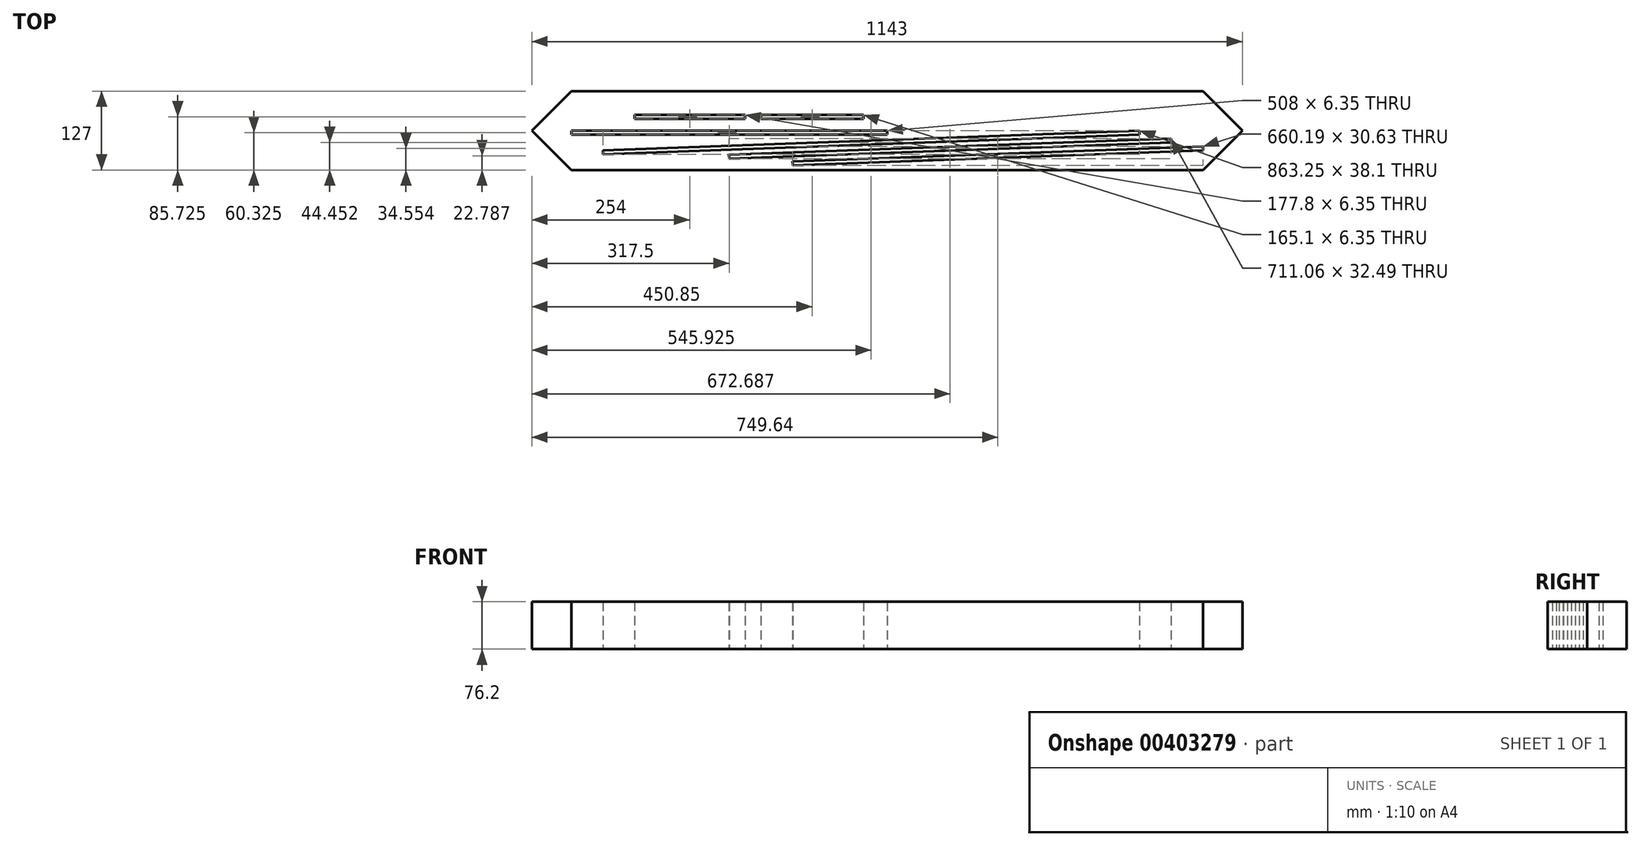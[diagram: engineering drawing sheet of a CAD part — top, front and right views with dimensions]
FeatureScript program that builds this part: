
annotation { "Feature Type Name" : "Feature", "Feature Type Description" : "" }
export const myFeature = defineFeature(function(context is Context, id is Id, definition is map)
    precondition{}
    {
        {
            var Q0;
            Q0=qCreatedBy(makeId("Top.planeOp"),FACE);
            var sketch = newSketch(context, id + "F0", { "sketchPlane" : qUnion([Q0])});
            skLineSegment(sketch, "E0.bottom", {"start": v(-508, 0) * mm, "end": v(508, 0) * mm});
            skLineSegment(sketch, "E0.top", {"start": v(-508, -127) * mm, "end": v(508, -127) * mm});
            skLineSegment(sketch, "E0.left", {"start": v(-508, 0) * mm, "end": v(-508, -127) * mm});
            skLineSegment(sketch, "E0.right", {"start": v(508, 0) * mm, "end": v(508, -127) * mm});
            skPoint(sketch, "E1", {"position": v(-508, -63.5) * mm});
            skPoint(sketch, "E2", {"position": v(508, -63.5) * mm});
            skLineSegment(sketch, "E3", {"start": v(-508, -63.5) * mm, "end": v(508, -63.5) * mm});
            skLineSegment(sketch, "E4", {"start": v(-508, -63.5) * mm, "end": v(-571.5, -63.5) * mm});
            skLineSegment(sketch, "E5", {"start": v(508, -63.5) * mm, "end": v(571.5, -63.5) * mm});
            skLineSegment(sketch, "E6", {"start": v(-571.5, -63.5) * mm, "end": v(-508, 0) * mm});
            skLineSegment(sketch, "E7", {"start": v(-571.5, -63.5) * mm, "end": v(-508, -127) * mm});
            skLineSegment(sketch, "E8", {"start": v(508, -127) * mm, "end": v(571.5, -63.5) * mm});
            skLineSegment(sketch, "E9", {"start": v(571.5, -63.5) * mm, "end": v(508, 0) * mm});
            skLineSegment(sketch, "E10.bottom", {"start": v(-406.4, -38.1) * mm, "end": v(-228.6, -38.1) * mm});
            skLineSegment(sketch, "E10.top", {"start": v(-406.4, -44.45) * mm, "end": v(-228.6, -44.45) * mm});
            skLineSegment(sketch, "E10.left", {"start": v(-406.4, -38.1) * mm, "end": v(-406.4, -44.45) * mm});
            skLineSegment(sketch, "E10.right", {"start": v(-228.6, -38.1) * mm, "end": v(-228.6, -44.45) * mm});
            skLineSegment(sketch, "E11.bottom", {"start": v(-203.2, -38.1) * mm, "end": v(-38.1, -38.1) * mm});
            skLineSegment(sketch, "E11.top", {"start": v(-203.2, -44.45) * mm, "end": v(-38.1, -44.45) * mm});
            skLineSegment(sketch, "E11.left", {"start": v(-203.2, -38.1) * mm, "end": v(-203.2, -44.45) * mm});
            skLineSegment(sketch, "E11.right", {"start": v(-38.1, -38.1) * mm, "end": v(-38.1, -44.45) * mm});
            skLineSegment(sketch, "E12.bottom", {"start": v(-508, -63.5) * mm, "end": v(0, -63.5) * mm});
            skLineSegment(sketch, "E12.top", {"start": v(-508, -69.85) * mm, "end": v(0, -69.85) * mm});
            skLineSegment(sketch, "E12.left", {"start": v(-508, -63.5) * mm, "end": v(-508, -69.85) * mm});
            skLineSegment(sketch, "E12.right", {"start": v(0, -63.5) * mm, "end": v(0, -69.85) * mm});
            skLineSegment(sketch, "E13", {"start": v(-457.2, -95.25) * mm, "end": v(405.82, -63.5) * mm});
            skLineSegment(sketch, "E14", {"start": v(-456.97, -101.6) * mm, "end": v(406.05, -69.85) * mm});
            skLineSegment(sketch, "E15", {"start": v(406.05, -69.85) * mm, "end": v(405.82, -63.5) * mm});
            skLineSegment(sketch, "E16", {"start": v(-457.2, -95.25) * mm, "end": v(-456.97, -101.6) * mm});
            skLineSegment(sketch, "E17", {"start": v(-254, -108.7) * mm, "end": v(456.72, -82.54) * mm});
            skLineSegment(sketch, "E18", {"start": v(456.72, -82.54) * mm, "end": v(456.49, -76.2) * mm});
            skLineSegment(sketch, "E19", {"start": v(456.49, -76.2) * mm, "end": v(-254.34, -102.35) * mm});
            skLineSegment(sketch, "E20", {"start": v(-254, -108.7) * mm, "end": v(-254.34, -102.35) * mm});
            skLineSegment(sketch, "E21", {"start": v(-151.72, -119.53) * mm, "end": v(508.23, -95.25) * mm});
            skLineSegment(sketch, "E22", {"start": v(508.23, -95.25) * mm, "end": v(508, -88.9) * mm});
            skLineSegment(sketch, "E23", {"start": v(508, -88.9) * mm, "end": v(-151.95, -113.18) * mm});
            skLineSegment(sketch, "E24", {"start": v(-151.95, -113.18) * mm, "end": v(-151.72, -119.53) * mm});
            skSolve(sketch);
        }
        {
            var Q0;
            Q0 = qSketchRegion(id + "F0", true);
            extrude(context, id + "F1", {"entities" : qUnion([Q0]), "depth" : 76.2 * mm});
        }
    });
